# Revit family: Magnuson-Sei-CoatHookStrip+
name_source: partatom
category: Furniture
units: mm (PartAtom-declared; Revit-internal decimal feet)

## family parameters
Cut with Voids When Loaded = No
Host = Face
Room Calculation Point = No
Shared = No

## types (2) — shared parameters
Assembly Code = E2020200
Default Elevation = 48"
End Dist = 1"
Frame Finish = MAG - Textured painted steel
Hook Finish = MAG - Textured painted steel
Keynote = 12500
Low Emitting Finish = Yes
Low Emitting Material = Yes
Manufacturer = Magnuson Group
Product Documentation Link = https://magnusongroup.com
Revit Model Built By = https://servex-us.com
Salvage or Reuse = Yes
Type Comments = Coat Hook Strip
URL = www.magnusongroup.com
zero-valued in all types: Percentage of Recycled Content

## per-type parameters (varying)
| type | Description | Hook Qty | Width | x |
| SEI-20 | Hook strip with three epoxy coated steel hat and coat hooks | 3 | 17 11/16" | Yes |
| SEI-10 | Hook strip with two epoxy coated steel hat and coat hooks | 2 | 9 27/32" | No |

note: column(s) folded — value = type name in every type: Model

## geometry (parser evidence)
native form markers: Sweep x5
no freeform markers — native parametric forms only
